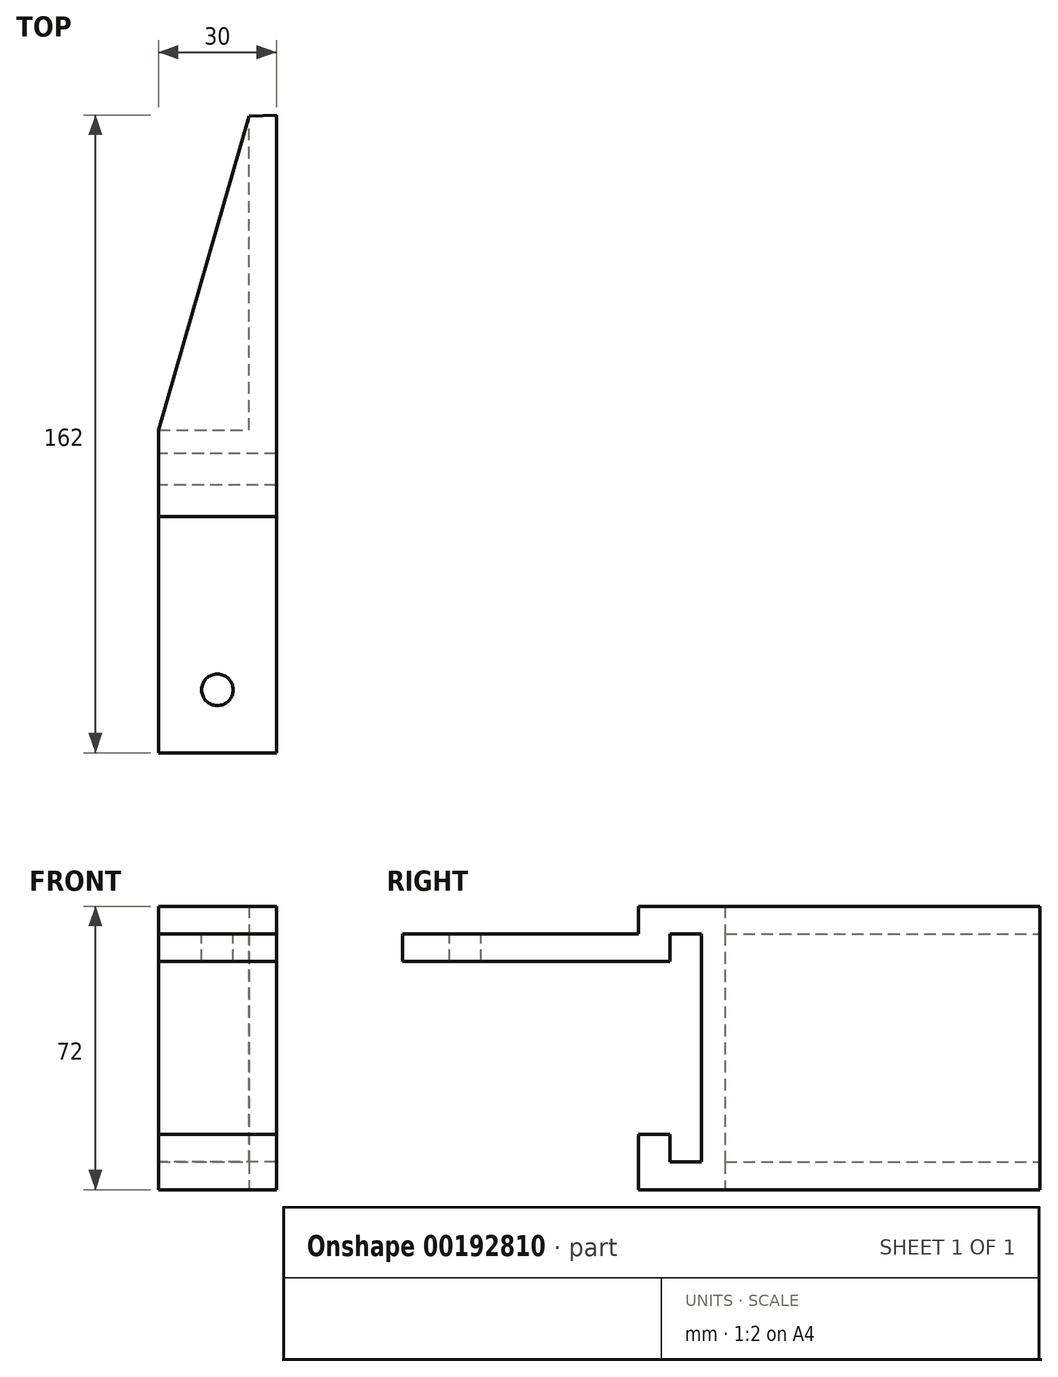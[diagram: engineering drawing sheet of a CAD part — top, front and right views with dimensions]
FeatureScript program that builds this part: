
annotation { "Feature Type Name" : "Feature", "Feature Type Description" : "" }
export const myFeature = defineFeature(function(context is Context, id is Id, definition is map)
    precondition{}
    {
        {
            var Q0;
            Q0=qCreatedBy(makeId("Top.planeOp"),FACE);
            var sketch = newSketch(context, id + "F0", { "sketchPlane" : qUnion([Q0])});
            skLineSegment(sketch, "E0.bottom", {"start": v(-30, 0) * mm, "end": v(0, 0) * mm});
            skLineSegment(sketch, "E0.top", {"start": v(-30, 22) * mm, "end": v(0, 22) * mm});
            skLineSegment(sketch, "E0.left", {"start": v(-30, 0) * mm, "end": v(-30, 22) * mm});
            skLineSegment(sketch, "E0.right", {"start": v(0, 0) * mm, "end": v(0, 22) * mm});
            skLineSegment(sketch, "E1", {"start": v(0, 22) * mm, "end": v(0, 102) * mm});
            skLineSegment(sketch, "E2", {"start": v(-30, 22) * mm, "end": v(-7, 101.72) * mm});
            skLineSegment(sketch, "E3", {"start": v(-7, 101.72) * mm, "end": v(0, 102) * mm});
            skSolve(sketch);
        }
        {
            var Q0;
            Q0 = qSketchRegion(id + "F0", true);
            extrude(context, id + "F1", {"entities" : qUnion([Q0]), "depth" : 72 * mm});
        }
        {
            var Q0;
            Q0=makeQuery(id+"F1.opExtrude","CAP_FACE",FACE,{"disambiguationData":[OSD([sQuery(id+"F0.wireOp",EDGE,"E0.bottom"),sQuery(id+"F0.wireOp",EDGE,"E0.left"),sQuery(id+"F0.wireOp",EDGE,"E0.right"),sQuery(id+"F0.wireOp",EDGE,"E1"),sQuery(id+"F0.wireOp",EDGE,"xLnjd96q-PZ0L-wumJ-MDfw-arIAMcblvKvu")])],"isStart":false});
            var sketch = newSketch(context, id + "F2", { "sketchPlane" : qUnion([Q0])});
            skLineSegment(sketch, "E4", {"start": v(-30, 22) * mm, "end": v(-7, 22) * mm});
            skLineSegment(sketch, "E5", {"start": v(-7, 22) * mm, "end": v(-7, 101.72) * mm});
            skLineSegment(sketch, "E6", {"start": v(-7, 101.72) * mm, "end": v(-30, 22) * mm});
            skSolve(sketch);
        }
        {
            var Q0;
            Q0 = qSketchRegion(id + "F2", true);
            extrude(context, id + "F3", {"entities" : qUnion([Q0]), "operationType" : NewBodyOperationType.REMOVE, "endBound" : BoundingType.THROUGH_ALL, "oppositeDirection" : true, "depth" : 25 * mm});
        }
        {
            var Q0;
            Q0 = qSketchRegion(id + "F2", true);
            extrude(context, id + "F4", {"entities" : qUnion([Q0]), "operationType" : NewBodyOperationType.ADD, "oppositeDirection" : true, "depth" : 7 * mm});
        }
        {
            var Q0;
            Q0=makeQuery(id+"F1.opExtrude","CAP_FACE",FACE,{"disambiguationData":[OSD([sQuery(id+"F0.wireOp",EDGE,"E0.bottom"),sQuery(id+"F0.wireOp",EDGE,"E0.left"),sQuery(id+"F0.wireOp",EDGE,"E0.right"),sQuery(id+"F0.wireOp",EDGE,"E1"),sQuery(id+"F0.wireOp",EDGE,"xLnjd96q-PZ0L-wumJ-MDfw-arIAMcblvKvu")])],"isStart":true});
            var sketch = newSketch(context, id + "F5", { "sketchPlane" : qUnion([Q0])});
            skLineSegment(sketch, "E7", {"start": v(-7, -22) * mm, "end": v(-7, -22) * mm});
            skLineSegment(sketch, "E8", {"start": v(-7, -22) * mm, "end": v(-30, -22) * mm});
            skLineSegment(sketch, "E9", {"start": v(-30, -22) * mm, "end": v(-7, -101.72) * mm});
            skLineSegment(sketch, "E10", {"start": v(-7, -101.72) * mm, "end": v(-7, -22) * mm});
            skSolve(sketch);
        }
        {
            var Q0;
            Q0 = qSketchRegion(id + "F5", true);
            extrude(context, id + "F6", {"entities" : qUnion([Q0]), "operationType" : NewBodyOperationType.ADD, "oppositeDirection" : true, "depth" : 7 * mm});
        }
        {
            var Q0;
            Q0=makeQuery(id+"F1.opExtrude","SWEPT_FACE",FACE,{"disambiguationData":[OSD([sQuery(id+"F0.wireOp",EDGE,"E0.left")])]});
            var sketch = newSketch(context, id + "F7", { "sketchPlane" : qUnion([Q0])});
            skLineSegment(sketch, "E11.bottom", {"start": v(-16, 65) * mm, "end": v(-8, 65) * mm});
            skLineSegment(sketch, "E11.top", {"start": v(-16, 7) * mm, "end": v(-8, 7) * mm});
            skLineSegment(sketch, "E11.left", {"start": v(-16, 65) * mm, "end": v(-16, 7) * mm});
            skLineSegment(sketch, "E11.right", {"start": v(-8, 65) * mm, "end": v(-8, 7) * mm});
            skLineSegment(sketch, "E12.bottom", {"start": v(-8, 58) * mm, "end": v(0, 58) * mm});
            skLineSegment(sketch, "E12.top", {"start": v(-8, 14) * mm, "end": v(0, 14) * mm});
            skLineSegment(sketch, "E12.left", {"start": v(-8, 58) * mm, "end": v(-8, 14) * mm});
            skLineSegment(sketch, "E12.right", {"start": v(0, 58) * mm, "end": v(0, 14) * mm});
            skSolve(sketch);
        }
        {
            var Q0;
            Q0 = qSketchRegion(id + "F7", true);
            extrude(context, id + "F8", {"entities" : qUnion([Q0]), "operationType" : NewBodyOperationType.REMOVE, "endBound" : BoundingType.THROUGH_ALL, "oppositeDirection" : true, "depth" : 25 * mm});
        }
        {
            var Q0;
            {var subQ3=sQuery(id+"F0.wireOp",EDGE,"E0.bottom");Q0=makeQuery(id+"F8.boolean.opBoolean","SPLIT",FACE,{"disambiguationData":[TD([makeQuery(id+"F8.opExtrude","SWEPT_FACE",FACE,{"disambiguationData":[OSD([sQuery(id+"F7.wireOp",EDGE,"E12.bottom")])]})])],"derivedFrom":makeQuery(id+"F1.opExtrude","SWEPT_FACE",FACE,{"disambiguationData":[OSD([subQ3])]})});}
            var sketch = newSketch(context, id + "F9", { "sketchPlane" : qUnion([Q0])});
            skLineSegment(sketch, "E13.bottom", {"start": v(-30, 58) * mm, "end": v(0, 58) * mm});
            skLineSegment(sketch, "E13.top", {"start": v(-30, 65) * mm, "end": v(0, 65) * mm});
            skLineSegment(sketch, "E13.left", {"start": v(-30, 58) * mm, "end": v(-30, 65) * mm});
            skLineSegment(sketch, "E13.right", {"start": v(0, 58) * mm, "end": v(0, 65) * mm});
            skSolve(sketch);
        }
        {
            var Q0;
            Q0 = qSketchRegion(id + "F9", true);
            extrude(context, id + "F10", {"entities" : qUnion([Q0]), "operationType" : NewBodyOperationType.ADD, "depth" : 60 * mm});
        }
        {
            var Q0;
            Q0=makeQuery(id+"F10.opExtrude","SWEPT_FACE",FACE,{"disambiguationData":[OSD([sQuery(id+"F9.wireOp",EDGE,"E13.top")])]});
            var sketch = newSketch(context, id + "F11", { "sketchPlane" : qUnion([Q0])});
            skCircle(sketch, "E14", {"center": v(-15, -44) * mm, "radius": 4 * mm});
            skPoint(sketch, "E14.centerSnap0", {"position": v(-15, -60) * mm});
            skSolve(sketch);
        }
        {
            var Q0;
            Q0 = qSketchRegion(id + "F11", true);
            extrude(context, id + "F12", {"entities" : qUnion([Q0]), "operationType" : NewBodyOperationType.REMOVE, "endBound" : BoundingType.THROUGH_ALL, "oppositeDirection" : true, "depth" : 25 * mm});
        }
    });
